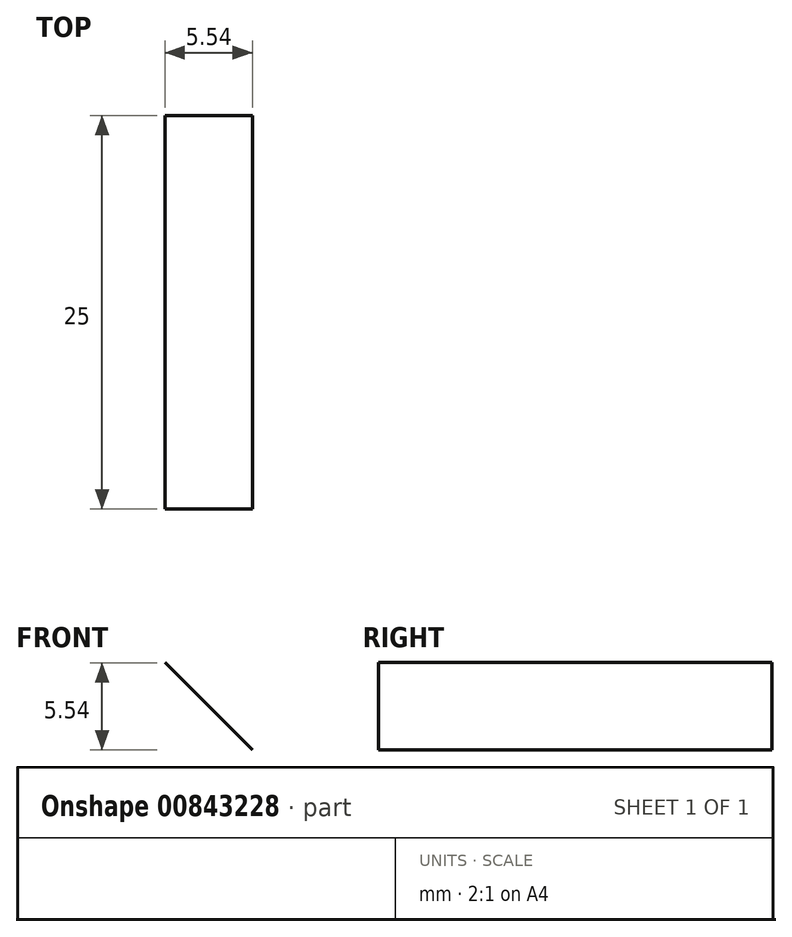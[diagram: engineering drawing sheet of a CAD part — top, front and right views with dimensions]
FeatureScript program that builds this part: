
annotation { "Feature Type Name" : "Feature", "Feature Type Description" : "" }
export const myFeature = defineFeature(function(context is Context, id is Id, definition is map)
    precondition{}
    {
        {
            var Q0;
            Q0=qCreatedBy(makeId("Front.planeOp"),FACE);
            var sketch = newSketch(context, id + "F0", { "sketchPlane" : qUnion([Q0])});
            skLineSegment(sketch, "E0.bottom", {"start": v(-38.32, 35.87) * mm, "end": v(39.58, 35.87) * mm});
            skLineSegment(sketch, "E0.top", {"start": v(-38.32, -41.74) * mm, "end": v(39.58, -41.74) * mm});
            skLineSegment(sketch, "E0.left", {"start": v(-38.32, 35.87) * mm, "end": v(-38.32, -41.74) * mm});
            skLineSegment(sketch, "E0.right", {"start": v(39.58, 35.87) * mm, "end": v(39.58, -41.74) * mm});
            skLineSegment(sketch, "E1.bottom", {"start": v(-43.86, 41.41) * mm, "end": v(36.36, 41.41) * mm});
            skLineSegment(sketch, "E1.top", {"start": v(-43.86, -37.17) * mm, "end": v(36.36, -37.17) * mm});
            skLineSegment(sketch, "E1.left", {"start": v(-43.86, 41.41) * mm, "end": v(-43.86, -37.17) * mm});
            skLineSegment(sketch, "E1.right", {"start": v(36.36, 41.41) * mm, "end": v(36.36, -37.17) * mm});
            skLineSegment(sketch, "E2", {"start": v(-38.32, 35.87) * mm, "end": v(-43.86, 41.41) * mm});
            skLineSegment(sketch, "E3", {"start": v(39.58, 35.87) * mm, "end": v(36.36, 41.41) * mm});
            skLineSegment(sketch, "E4", {"start": v(-38.32, -41.74) * mm, "end": v(-43.86, -37.17) * mm});
            skLineSegment(sketch, "E5", {"start": v(39.58, -41.74) * mm, "end": v(36.36, -37.17) * mm});
            skLineSegment(sketch, "E6", {"start": v(-13.53, -30) * mm, "end": v(14.51, -30) * mm});
            skLineSegment(sketch, "E7", {"start": v(14.51, -30) * mm, "end": v(14.51, -53.15) * mm});
            skLineSegment(sketch, "E8", {"start": v(14.51, -53.15) * mm, "end": v(-14.18, -53.15) * mm});
            skLineSegment(sketch, "E9", {"start": v(-14.18, -53.15) * mm, "end": v(-13.53, -30) * mm});
            skLineSegment(sketch, "E10", {"start": v(-14.18, -53.15) * mm, "end": v(-33.1, -68.15) * mm});
            skLineSegment(sketch, "E11", {"start": v(-33.1, -68.15) * mm, "end": v(33.1, -68.15) * mm});
            skLineSegment(sketch, "E12", {"start": v(33.1, -68.15) * mm, "end": v(14.51, -53.15) * mm});
            skLineSegment(sketch, "E13", {"start": v(35.38, -68.15) * mm, "end": v(23.97, -45.65) * mm});
            skLineSegment(sketch, "E14", {"start": v(23.97, -45.65) * mm, "end": v(14.51, -53.15) * mm});
            skLineSegment(sketch, "E15", {"start": v(-33.1, -68.15) * mm, "end": v(-25.6, -45.65) * mm});
            skLineSegment(sketch, "E16", {"start": v(-25.6, -45.65) * mm, "end": v(-14.18, -53.15) * mm});
            skText(sketch, "E17", { "text": "Hp", "fontName": "OpenSans-Regular.ttf"});
            const initialGuessF0  = {"E17": [-0.00799, -0.04174, 1, 0, 0.00457]};
            skSetInitialGuess(sketch, initialGuessF0);
            skSolve(sketch);
        }
        {
            var Q0;
            Q0=sQuery(id+"F0.wireOp",EDGE,"E2");
            extrude(context, id + "F1", {"bodyType" : ToolBodyType.SURFACE, "surfaceEntities" : qUnion([Q0]), "depth" : 25 * mm, "offsetDistance" : 25 * mm});
        }
    });
